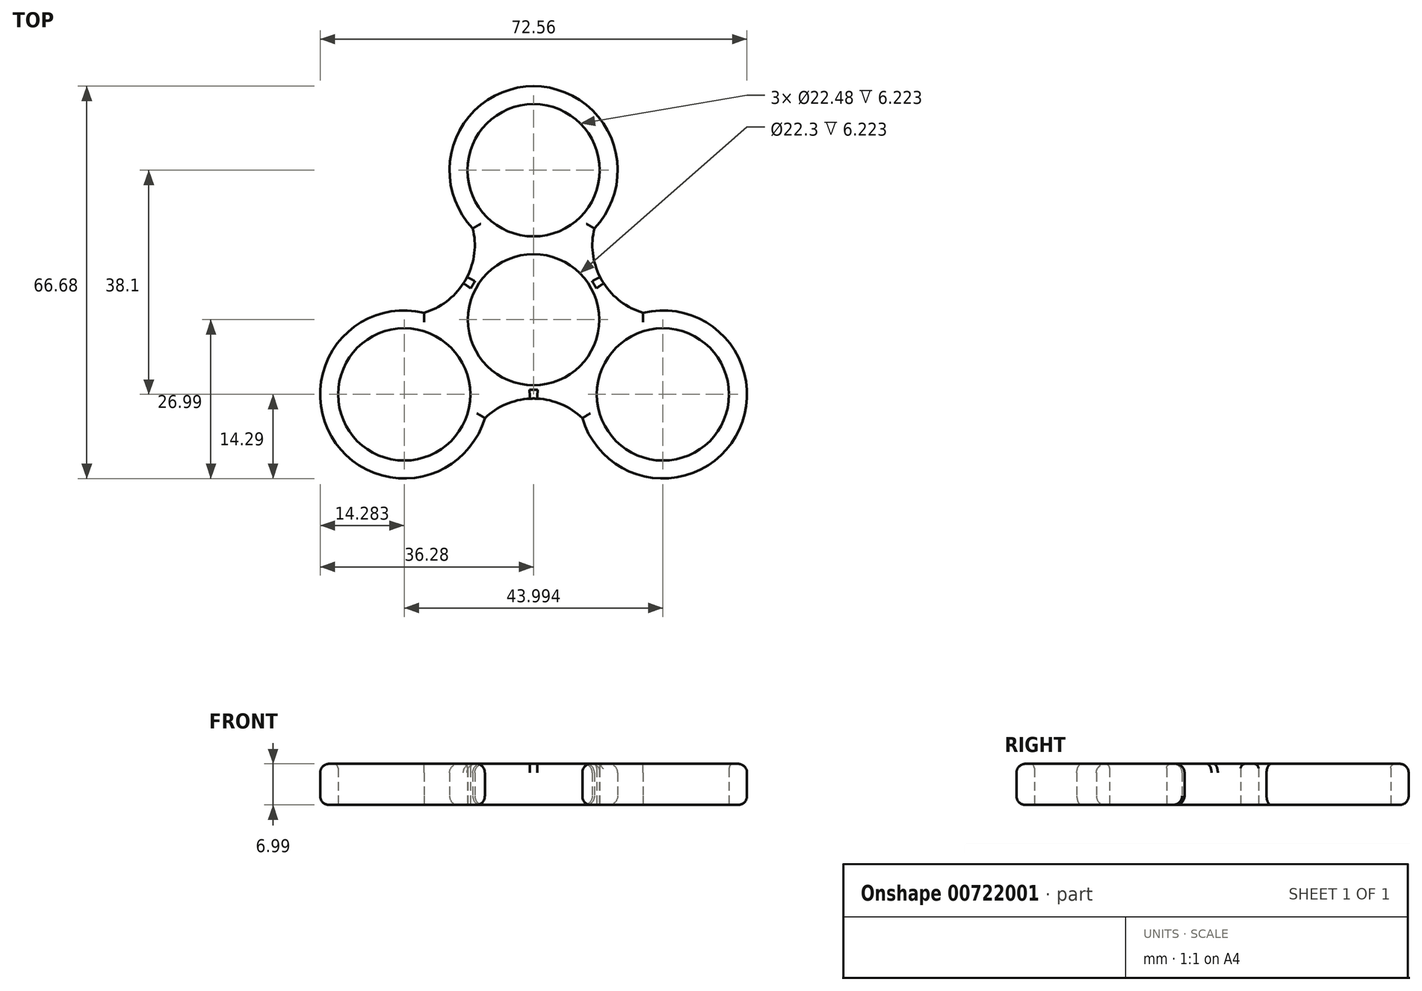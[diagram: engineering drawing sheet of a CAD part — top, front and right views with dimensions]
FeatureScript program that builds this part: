
annotation { "Feature Type Name" : "Feature", "Feature Type Description" : "" }
export const myFeature = defineFeature(function(context is Context, id is Id, definition is map)
    precondition{}
    {
        {
            var Q0;
            Q0=qCreatedBy(makeId("Top.planeOp"),FACE);
            var sketch = newSketch(context, id + "F0", { "sketchPlane" : qUnion([Q0])});
            skCircle(sketch, "E0", {"center": v(0, 0) * mm, "radius": 10.99 * mm, "construction": true});
            skCircle(sketch, "E1", {"center": v(0, 0) * mm, "radius": 25.4 * mm, "construction": true});
            skLineSegment(sketch, "E2", {"start": v(0, 0) * mm, "end": v(0, 25.4) * mm, "construction": true});
            skLineSegment(sketch, "E3", {"start": v(0, 0) * mm, "end": v(-22, -12.7) * mm, "construction": true});
            skLineSegment(sketch, "E4", {"start": v(-22, -12.7) * mm, "end": v(0, 0) * mm, "construction": true});
            skLineSegment(sketch, "E5", {"start": v(0, 0) * mm, "end": v(22, -12.7) * mm, "construction": true});
            skCircle(sketch, "E6", {"center": v(-22, -12.7) * mm, "radius": 11.11 * mm, "construction": true});
            skCircle(sketch, "E7", {"center": v(22, -12.7) * mm, "radius": 11.11 * mm, "construction": true});
            skCircle(sketch, "E8", {"center": v(0, 25.4) * mm, "radius": 11.11 * mm, "construction": true});
            skArc(sketch, "E9", {"start": v(-18.62, 1.18) * mm, "mid": v(-34.37, -19.84) * mm, "end": v(-8.29, -16.72) * mm});
            skArc(sketch, "E10", {"start": v(8.29, -16.72) * mm, "mid": v(34.37, -19.84) * mm, "end": v(18.62, 1.18) * mm});
            skArc(sketch, "E11", {"start": v(10.34, 15.54) * mm, "mid": v(0, 39.69) * mm, "end": v(-10.34, 15.54) * mm});
            skArc(sketch, "E12", {"start": v(-18.62, 1.18) * mm, "mid": v(-11.6, 6.7) * mm, "end": v(-10.34, 15.54) * mm});
            skArc(sketch, "E13.1.0", {"start": v(8.29, -16.72) * mm, "mid": v(0, -13.4) * mm, "end": v(-8.29, -16.72) * mm});
            skArc(sketch, "E13.2.0", {"start": v(10.34, 15.54) * mm, "mid": v(11.6, 6.7) * mm, "end": v(18.62, 1.18) * mm});
            skSolve(sketch);
        }
        {
            var Q0;
            Q0 = qSketchRegion(id + "F0", true);
            extrude(context, id + "F1", {"entities" : qUnion([Q0]), "depth" : 7 * mm, "offsetDistance" : 25.4 * mm});
        }
        {
            var Q0;
            Q0=makeQuery(id+"F1.opExtrude","CAP_FACE",FACE,{"disambiguationData":[OSD([sQuery(id+"F0.wireOp",EDGE,"E9"),sQuery(id+"F0.wireOp",EDGE,"E10"),sQuery(id+"F0.wireOp",EDGE,"E11"),sQuery(id+"F0.wireOp",EDGE,"E12"),sQuery(id+"F0.wireOp",EDGE,"E13.1.0"),sQuery(id+"F0.wireOp",EDGE,"E13.2.0")])],"isStart":true});
            var sketch = newSketch(context, id + "F2", { "sketchPlane" : qUnion([Q0])});
            skCircle(sketch, "E14", {"center": v(0, 0) * mm, "radius": 11.15 * mm});
            skCircle(sketch, "E15", {"center": v(-22, 12.7) * mm, "radius": 11.24 * mm});
            skCircle(sketch, "E16", {"center": v(22, 12.7) * mm, "radius": 11.24 * mm});
            skCircle(sketch, "E17", {"center": v(0, -25.4) * mm, "radius": 11.24 * mm});
            skSolve(sketch);
        }
        {
            var Q0;
            Q0 = qSketchRegion(id + "F2", true);
            extrude(context, id + "F3", {"entities" : qUnion([Q0]), "operationType" : NewBodyOperationType.REMOVE, "oppositeDirection" : true, "depth" : 25.4 * mm, "offsetDistance" : 25.4 * mm});
        }
        {
            var Q0;
            Q0=makeQuery(id+"F3.boolean.opBoolean","INTERSECT",EDGE,{"derivedFrom":[makeQuery(id+"F1.opExtrude","CAP_FACE",FACE,{"disambiguationData":[OSD([sQuery(id+"F0.wireOp",EDGE,"E9"),sQuery(id+"F0.wireOp",EDGE,"E10"),sQuery(id+"F0.wireOp",EDGE,"E11"),sQuery(id+"F0.wireOp",EDGE,"E12"),sQuery(id+"F0.wireOp",EDGE,"E13.1.0"),sQuery(id+"F0.wireOp",EDGE,"E13.2.0")])],"isStart":false}),makeQuery(id+"F3.opExtrude","SWEPT_FACE",FACE,{"disambiguationData":[OSD([sQuery(id+"F2.wireOp",EDGE,"E16")])]})]});
            var Q1;
            Q1=makeQuery(id+"F3.boolean.opBoolean","INTERSECT",EDGE,{"derivedFrom":[makeQuery(id+"F1.opExtrude","CAP_FACE",FACE,{"disambiguationData":[OSD([sQuery(id+"F0.wireOp",EDGE,"E9"),sQuery(id+"F0.wireOp",EDGE,"E10"),sQuery(id+"F0.wireOp",EDGE,"E11"),sQuery(id+"F0.wireOp",EDGE,"E12"),sQuery(id+"F0.wireOp",EDGE,"E13.1.0"),sQuery(id+"F0.wireOp",EDGE,"E13.2.0")])],"isStart":false}),makeQuery(id+"F3.opExtrude","SWEPT_FACE",FACE,{"disambiguationData":[OSD([sQuery(id+"F2.wireOp",EDGE,"E14")])]})]});
            var Q2;
            Q2=makeQuery(id+"F3.boolean.opBoolean","INTERSECT",EDGE,{"derivedFrom":[makeQuery(id+"F1.opExtrude","CAP_FACE",FACE,{"disambiguationData":[OSD([sQuery(id+"F0.wireOp",EDGE,"E9"),sQuery(id+"F0.wireOp",EDGE,"E10"),sQuery(id+"F0.wireOp",EDGE,"E11"),sQuery(id+"F0.wireOp",EDGE,"E12"),sQuery(id+"F0.wireOp",EDGE,"E13.1.0"),sQuery(id+"F0.wireOp",EDGE,"E13.2.0")])],"isStart":false}),makeQuery(id+"F3.opExtrude","SWEPT_FACE",FACE,{"disambiguationData":[OSD([sQuery(id+"F2.wireOp",EDGE,"E15")])]})]});
            var Q3;
            Q3=makeQuery(id+"F3.boolean.opBoolean","INTERSECT",EDGE,{"derivedFrom":[makeQuery(id+"F1.opExtrude","CAP_FACE",FACE,{"disambiguationData":[OSD([sQuery(id+"F0.wireOp",EDGE,"E9"),sQuery(id+"F0.wireOp",EDGE,"E10"),sQuery(id+"F0.wireOp",EDGE,"E11"),sQuery(id+"F0.wireOp",EDGE,"E12"),sQuery(id+"F0.wireOp",EDGE,"E13.1.0"),sQuery(id+"F0.wireOp",EDGE,"E13.2.0")])],"isStart":false}),makeQuery(id+"F3.opExtrude","SWEPT_FACE",FACE,{"disambiguationData":[OSD([sQuery(id+"F2.wireOp",EDGE,"E17")])]})]});
            var Q4;
            Q4=makeQuery(id+"F3.boolean.opBoolean","COPY",EDGE,{"derivedFrom":makeQuery(id+"F3.opExtrude","CAP_EDGE",EDGE,{"disambiguationData":[OSD([sQuery(id+"F2.wireOp",EDGE,"E15")])],"isStart":true})});
            var Q5;
            Q5=makeQuery(id+"F3.boolean.opBoolean","COPY",EDGE,{"derivedFrom":makeQuery(id+"F3.opExtrude","CAP_EDGE",EDGE,{"disambiguationData":[OSD([sQuery(id+"F2.wireOp",EDGE,"E14")])],"isStart":true})});
            var Q6;
            Q6=makeQuery(id+"F3.boolean.opBoolean","COPY",EDGE,{"derivedFrom":makeQuery(id+"F3.opExtrude","CAP_EDGE",EDGE,{"disambiguationData":[OSD([sQuery(id+"F2.wireOp",EDGE,"E17")])],"isStart":true})});
            var Q7;
            Q7=makeQuery(id+"F3.boolean.opBoolean","COPY",EDGE,{"derivedFrom":makeQuery(id+"F3.opExtrude","CAP_EDGE",EDGE,{"disambiguationData":[OSD([sQuery(id+"F2.wireOp",EDGE,"E16")])],"isStart":true})});
            fillet(context, id + "F4", {"entities" : qUnion([Q0, Q1, Q2, Q3, Q4, Q5, Q6, Q7]), "radius" : 0.76 * mm, "tangentPropagation" : true, "allowEdgeOverflow" : false});
        }
        {
            var Q0;
            Q0=makeQuery(id+"F1.opExtrude","CAP_EDGE",EDGE,{"disambiguationData":[OSD([sQuery(id+"F0.wireOp",EDGE,"E11")])],"isStart":true});
            var Q1;
            Q1=makeQuery(id+"F1.opExtrude","CAP_EDGE",EDGE,{"disambiguationData":[OSD([sQuery(id+"F0.wireOp",EDGE,"E13.2.0")])],"isStart":true});
            var Q2;
            Q2=makeQuery(id+"F1.opExtrude","CAP_EDGE",EDGE,{"disambiguationData":[OSD([sQuery(id+"F0.wireOp",EDGE,"E10")])],"isStart":true});
            var Q3;
            Q3=makeQuery(id+"F1.opExtrude","CAP_EDGE",EDGE,{"disambiguationData":[OSD([sQuery(id+"F0.wireOp",EDGE,"E13.1.0")])],"isStart":true});
            var Q4;
            Q4=makeQuery(id+"F1.opExtrude","CAP_EDGE",EDGE,{"disambiguationData":[OSD([sQuery(id+"F0.wireOp",EDGE,"E9")])],"isStart":true});
            var Q5;
            Q5=makeQuery(id+"F1.opExtrude","CAP_EDGE",EDGE,{"disambiguationData":[OSD([sQuery(id+"F0.wireOp",EDGE,"E12")])],"isStart":true});
            var Q6;
            Q6=makeQuery(id+"F1.opExtrude","CAP_EDGE",EDGE,{"disambiguationData":[OSD([sQuery(id+"F0.wireOp",EDGE,"E12")])],"isStart":false});
            var Q7;
            Q7=makeQuery(id+"F1.opExtrude","CAP_EDGE",EDGE,{"disambiguationData":[OSD([sQuery(id+"F0.wireOp",EDGE,"E9")])],"isStart":false});
            var Q8;
            Q8=makeQuery(id+"F1.opExtrude","CAP_EDGE",EDGE,{"disambiguationData":[OSD([sQuery(id+"F0.wireOp",EDGE,"E13.1.0")])],"isStart":false});
            var Q9;
            Q9=makeQuery(id+"F1.opExtrude","CAP_EDGE",EDGE,{"disambiguationData":[OSD([sQuery(id+"F0.wireOp",EDGE,"E10")])],"isStart":false});
            var Q10;
            Q10=makeQuery(id+"F1.opExtrude","CAP_EDGE",EDGE,{"disambiguationData":[OSD([sQuery(id+"F0.wireOp",EDGE,"E13.2.0")])],"isStart":false});
            var Q11;
            Q11=makeQuery(id+"F1.opExtrude","CAP_EDGE",EDGE,{"disambiguationData":[OSD([sQuery(id+"F0.wireOp",EDGE,"E11")])],"isStart":false});
            fillet(context, id + "F5", {"entities" : qUnion([Q0, Q1, Q2, Q3, Q4, Q5, Q6, Q7, Q8, Q9, Q10, Q11]), "radius" : 1.52 * mm, "tangentPropagation" : true, "allowEdgeOverflow" : false});
        }
    });
